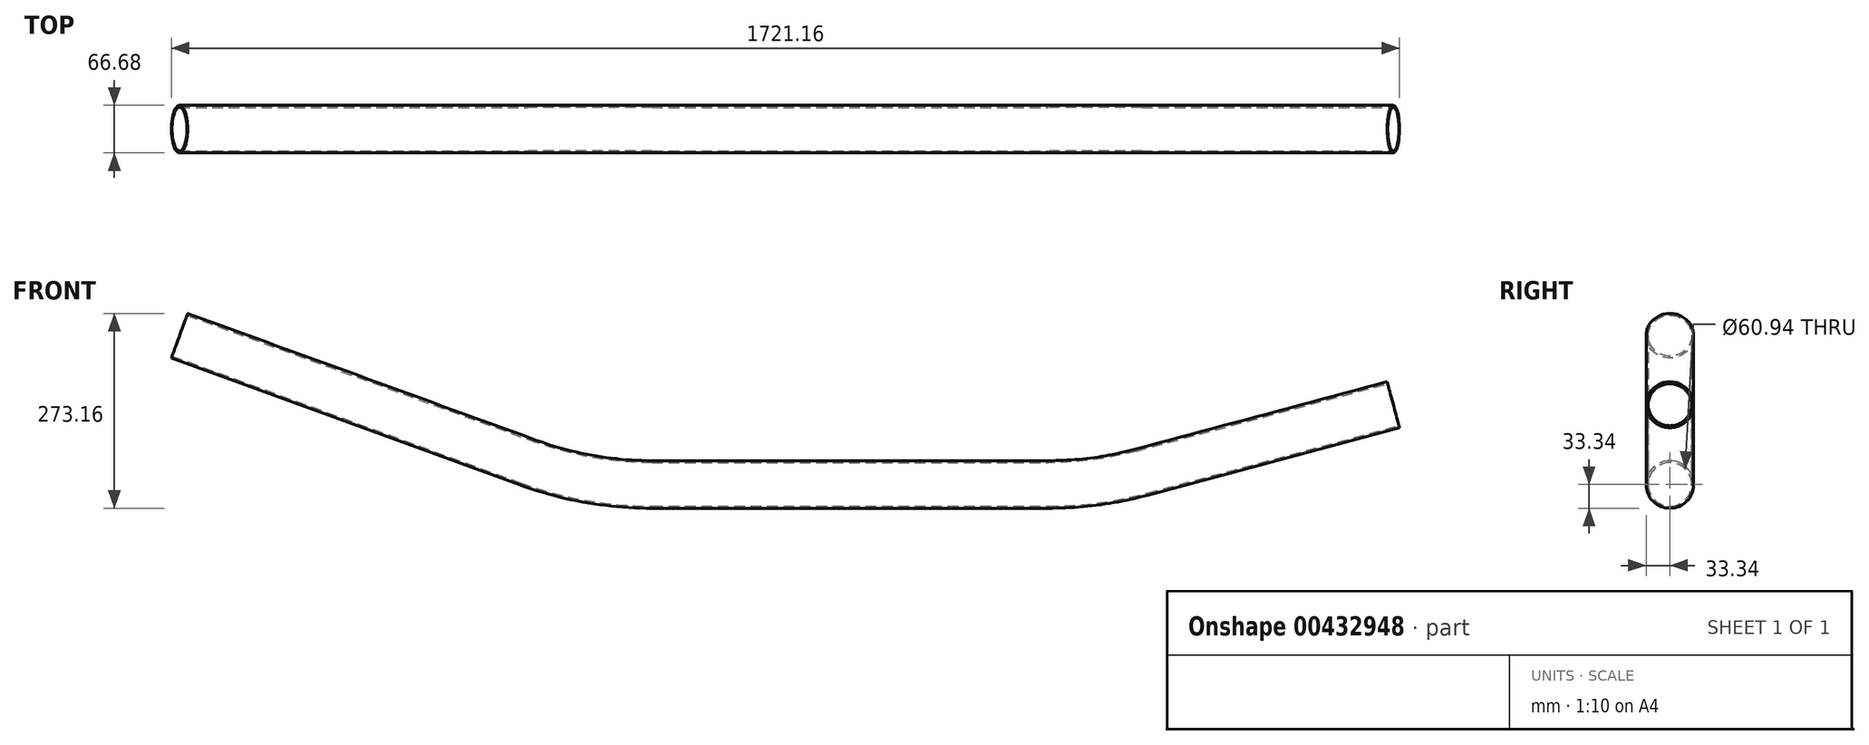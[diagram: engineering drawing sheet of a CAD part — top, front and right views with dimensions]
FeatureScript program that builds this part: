
annotation { "Feature Type Name" : "Feature", "Feature Type Description" : "" }
export const myFeature = defineFeature(function(context is Context, id is Id, definition is map)
    precondition{}
    {
        {
            var Q0;
            Q0=qCreatedBy(makeId("Front.planeOp"),FACE);
            var sketch = newSketch(context, id + "F0", { "sketchPlane" : qUnion([Q0])});
            skLineSegment(sketch, "E0", {"start": v(89.57, 0) * mm, "end": v(644.32, 0) * mm});
            skLineSegment(sketch, "E1", {"start": v(-84.17, 30.64) * mm, "end": v(-572.84, 208.5) * mm});
            skLineSegment(sketch, "E2", {"start": v(775.8, 17.3) * mm, "end": v(1128.29, 111.76) * mm});
            skPoint(sketch, "E3.visualSharp", {"position": v(0, 0) * mm});
            skArc(sketch, "E3.filletArc", {"start": v(-84.17, 30.64) * mm, "mid": v(1.36, 7.72) * mm, "end": v(89.57, 0) * mm});
            skPoint(sketch, "E4.visualSharp", {"position": v(711.2, 0) * mm});
            skArc(sketch, "E4.filletArc", {"start": v(644.32, 0) * mm, "mid": v(710.63, 4.35) * mm, "end": v(775.8, 17.3) * mm});
            skSolve(sketch);
        }
        {
            var Q0;
            Q0=sQuery(id+"F0.wireOp",VERTEX,"E1.end");
            var Q1;
            Q1=sQuery(id+"F0.wireOp",EDGE,"E1");
            cPlane(context, id + "F1", {"entities" : qUnion([Q0, Q1]), "cplaneType" : CPlaneType.LINE_POINT, "offset" : 25.4 * mm, "width" : 152.4 * mm, "height" : 152.4 * mm});
        }
        {
            var Q0;
            Q0=qCreatedBy(id+"F1.planeOp",FACE);
            var sketch = newSketch(context, id + "F2", { "sketchPlane" : qUnion([Q0])});
            skCircle(sketch, "E5", {"center": v(0, 0) * mm, "radius": 33.34 * mm});
            skSolve(sketch);
        }
        {
            var Q0;
            Q0=makeQuery(id+"F2.imprint","IMPRINT",FACE,{"disambiguationData":[TD([[makeQuery(id+"F2.imprint","IMPRINT",EDGE,{"derivedFrom":sQuery(id+"F2.wireOp",EDGE,"E5")}),1.0]])]});
            var Q1;
            Q1=sQuery(id+"F0.wireOp",EDGE,"E1");
            var Q2;
            Q2=sQuery(id+"F0.wireOp",EDGE,"E3.filletArc");
            var Q3;
            Q3=sQuery(id+"F0.wireOp",EDGE,"E0");
            var Q4;
            Q4=sQuery(id+"F0.wireOp",EDGE,"E4.filletArc");
            var Q5;
            Q5=sQuery(id+"F0.wireOp",EDGE,"E2");
            sweep(context, id + "F3", {"profiles" : qUnion([Q0]), "path" : qUnion([Q1, Q2, Q3, Q4, Q5])});
        }
        {
            var Q0;
            Q0=makeQuery(id+"F3.opSweep","CAP_FACE",FACE,{"disambiguationData":[OSD([sQuery(id+"F0.wireOp",VERTEX,"E1.end"),sQuery(id+"F2.wireOp",EDGE,"E5")])],"isStart":true});
            var Q1;
            Q1=makeQuery(id+"F3.opSweep","CAP_FACE",FACE,{"disambiguationData":[OSD([sQuery(id+"F0.wireOp",VERTEX,"E2.end"),sQuery(id+"F2.wireOp",EDGE,"E5")])],"isStart":false});
            shell(context, id + "F4", {"entities" : qUnion([Q0, Q1]), "thickness" : 2.87 * mm});
        }
    });
